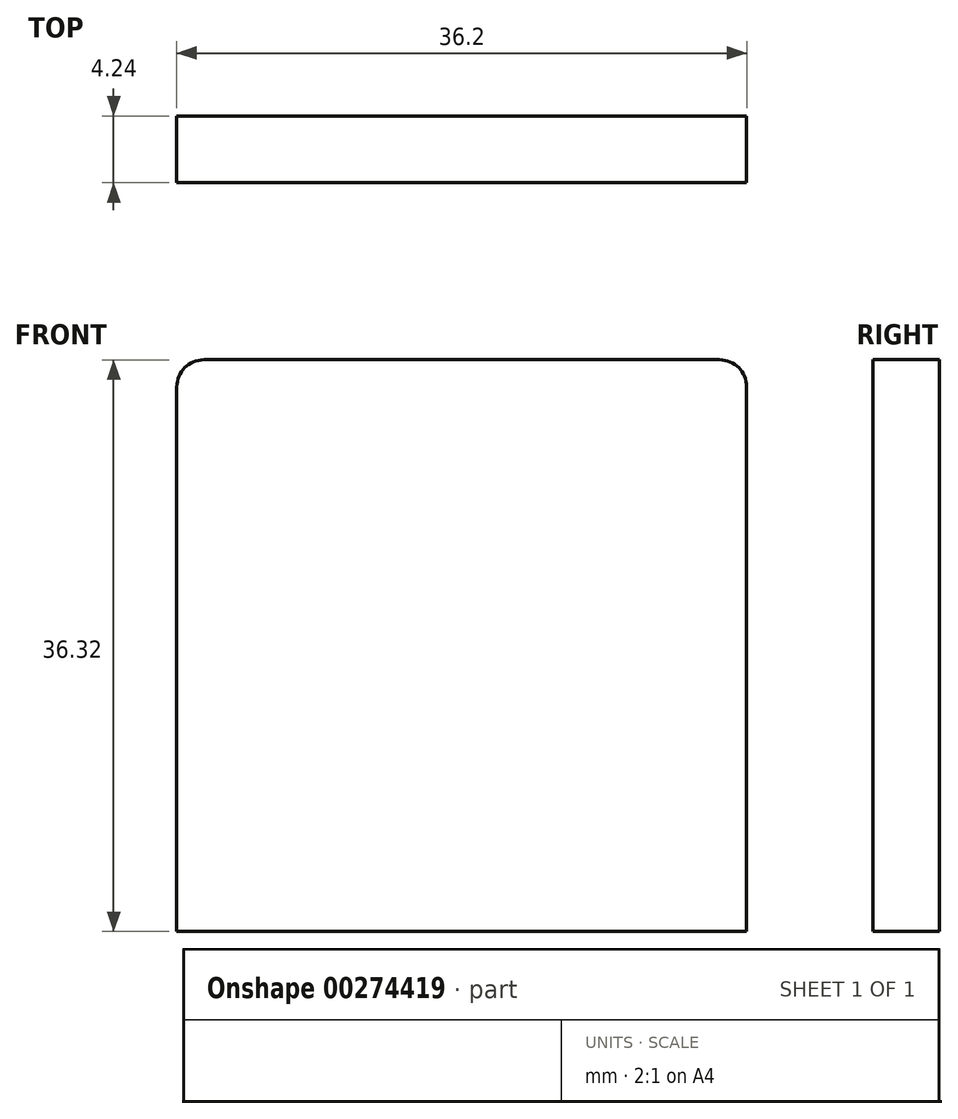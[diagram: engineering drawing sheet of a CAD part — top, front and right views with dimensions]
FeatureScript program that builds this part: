
annotation { "Feature Type Name" : "Feature", "Feature Type Description" : "" }
export const myFeature = defineFeature(function(context is Context, id is Id, definition is map)
    precondition{}
    {
        {
            var Q0;
            Q0=qCreatedBy(makeId("Front.planeOp"),FACE);
            var sketch = newSketch(context, id + "F0", { "sketchPlane" : qUnion([Q0])});
            skLineSegment(sketch, "E0.bottom", {"start": v(-18.1, 18.16) * mm, "end": v(18.1, 18.16) * mm});
            skLineSegment(sketch, "E0.top", {"start": v(-18.1, -18.16) * mm, "end": v(18.1, -18.16) * mm});
            skLineSegment(sketch, "E0.left", {"start": v(-18.1, 18.16) * mm, "end": v(-18.1, -18.16) * mm});
            skLineSegment(sketch, "E0.right", {"start": v(18.1, 18.16) * mm, "end": v(18.1, -18.16) * mm});
            skPoint(sketch, "E0.middle", {"position": v(0, 0) * mm});
            skSolve(sketch);
        }
        {
            var Q0;
            Q0=makeQuery(id+"F0.imprint","IMPRINT",FACE,{"disambiguationData":[TD([[makeQuery(id+"F0.imprint","IMPRINT",EDGE,{"derivedFrom":sQuery(id+"F0.wireOp",EDGE,"E0.bottom")}),-1.0]])]});
            extrude(context, id + "F1", {"entities" : qUnion([Q0]), "endBound" : BoundingType.SYMMETRIC, "depth" : 4.24 * mm});
        }
        {
            var Q0;
            Q0=makeQuery(id+"F1.opExtrude","SWEPT_EDGE",EDGE,{"disambiguationData":[OSD([sQuery(id+"F0.wireOp",EDGE,"E0.bottom"),sQuery(id+"F0.wireOp",EDGE,"E0.left")])]});
            var Q1;
            Q1=makeQuery(id+"F1.opExtrude","SWEPT_EDGE",EDGE,{"disambiguationData":[OSD([sQuery(id+"F0.wireOp",EDGE,"E0.bottom"),sQuery(id+"F0.wireOp",EDGE,"E0.right")])]});
            fillet(context, id + "F2", {"entities" : qUnion([Q0, Q1]), "radius" : 1.72 * mm, "tangentPropagation" : true, "allowEdgeOverflow" : false});
        }
    });
